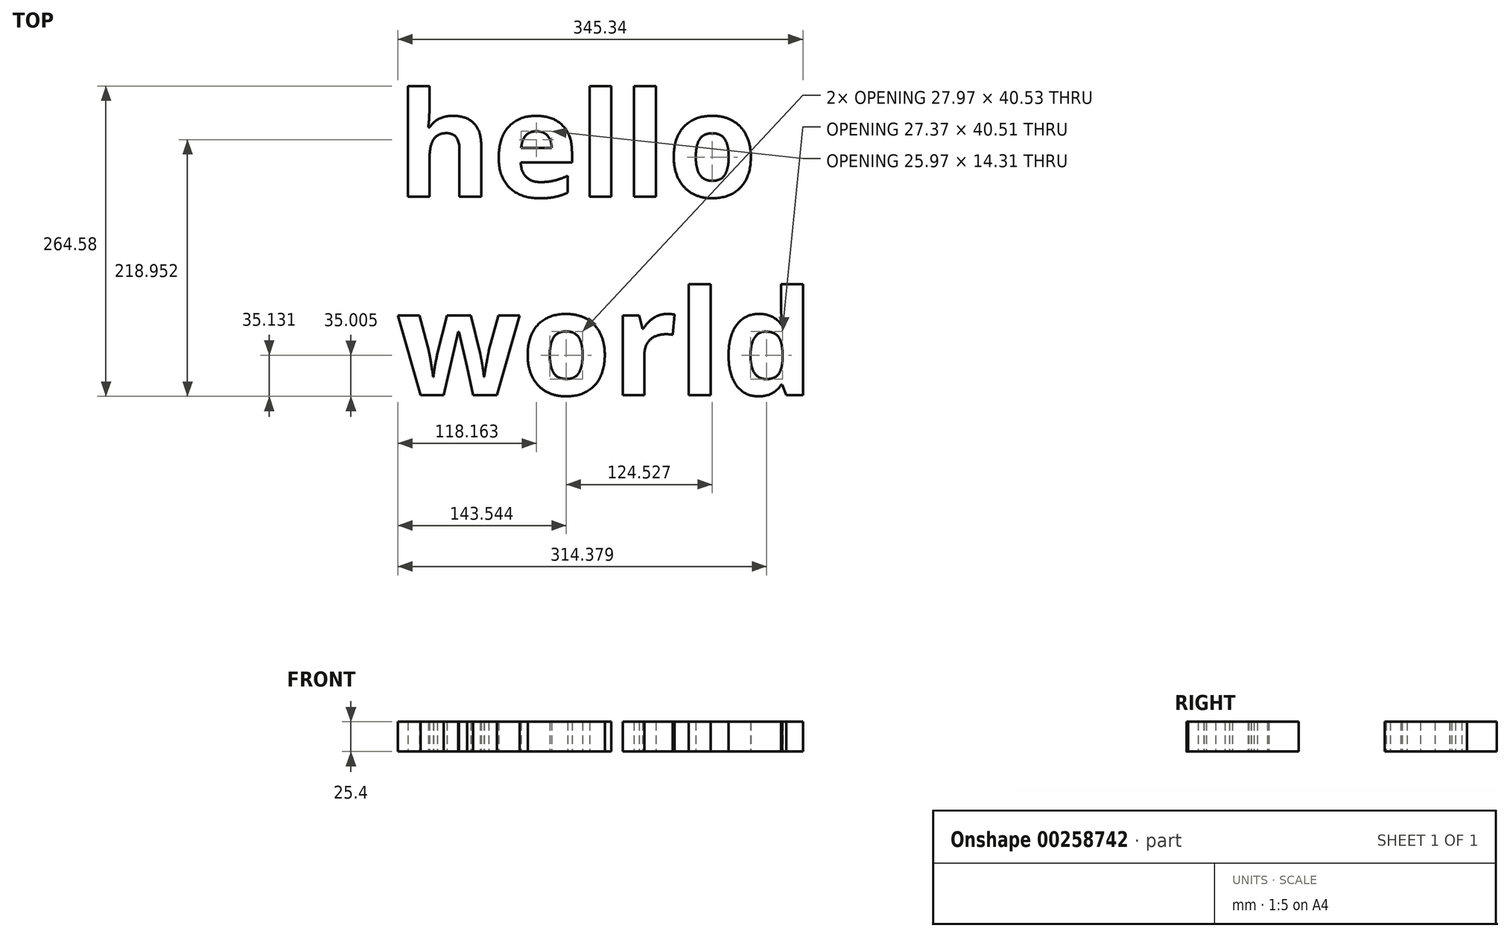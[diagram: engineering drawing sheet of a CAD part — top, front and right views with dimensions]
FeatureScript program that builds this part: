
annotation { "Feature Type Name" : "Feature", "Feature Type Description" : "" }
export const myFeature = defineFeature(function(context is Context, id is Id, definition is map)
    precondition{}
    {
        {
            var Q0;
            Q0=qCreatedBy(makeId("Top.planeOp"),FACE);
            var sketch = newSketch(context, id + "F0", { "sketchPlane" : qUnion([Q0])});
            skText(sketch, "E0", { "text": "hello\nworld", "fontName": "OpenSans-Bold.ttf"});
            const initialGuessF0  = {"E0": [-0.0666, -0.03916, 1, 0, 0.08945]};
            skSetInitialGuess(sketch, initialGuessF0);
            skSolve(sketch);
        }
        {
            var Q0;
            Q0 = qSketchRegion(id + "F0", true);
            extrude(context, id + "F1", {"entities" : qUnion([Q0]), "depth" : 25.4 * mm});
        }
    });
